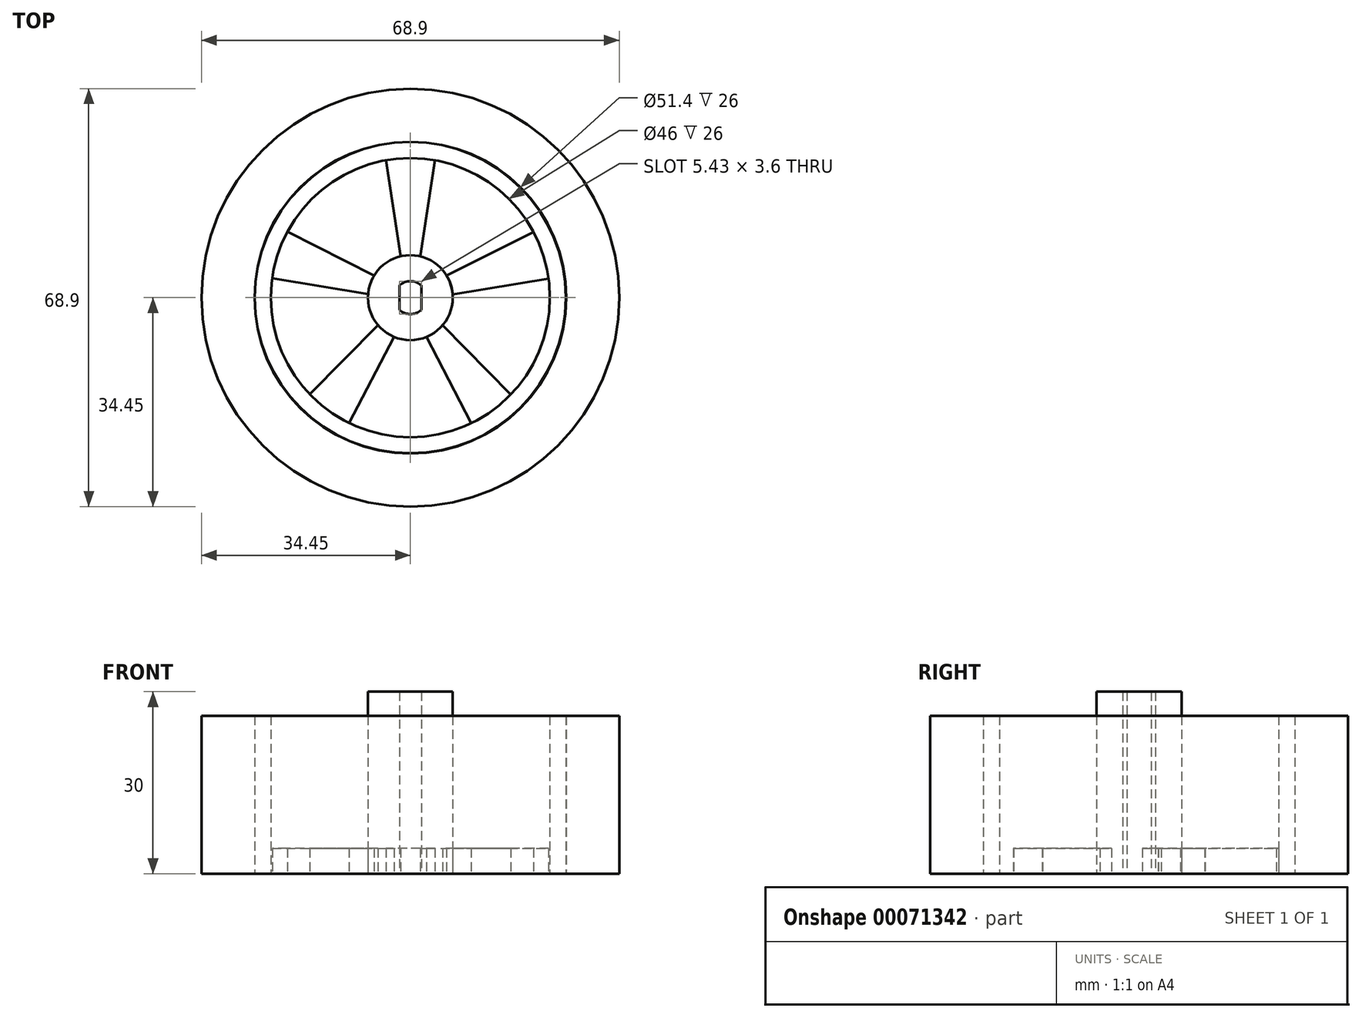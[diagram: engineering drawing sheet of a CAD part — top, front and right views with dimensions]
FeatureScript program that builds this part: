
annotation { "Feature Type Name" : "Feature", "Feature Type Description" : "" }
export const myFeature = defineFeature(function(context is Context, id is Id, definition is map)
    precondition{}
    {
        {
            var Q0;
            Q0=qCreatedBy(makeId("Top.planeOp"),FACE);
            var sketch = newSketch(context, id + "F0", { "sketchPlane" : qUnion([Q0])});
            skCircle(sketch, "E0", {"center": v(0, 0) * mm, "radius": 25.66 * mm});
            skCircle(sketch, "E1", {"center": v(0, 0) * mm, "radius": 23 * mm});
            skCircle(sketch, "E2", {"center": v(0, 0) * mm, "radius": 7 * mm});
            skArc(sketch, "E3", {"start": v(-1.8, -2.03) * mm, "mid": v(0, -2.71) * mm, "end": v(1.8, -2.03) * mm});
            skLineSegment(sketch, "E4.left", {"start": v(1.8, -2.03) * mm, "end": v(1.8, 2.03) * mm});
            skLineSegment(sketch, "E4.right", {"start": v(-1.8, -2.03) * mm, "end": v(-1.8, 2.03) * mm});
            skArc(sketch, "E5.trimOffspring", {"start": v(1.8, 2.03) * mm, "mid": v(0, 2.71) * mm, "end": v(-1.8, 2.03) * mm});
            skLineSegment(sketch, "E6", {"start": v(1.63, 6.8) * mm, "end": v(4.07, 22.64) * mm});
            skLineSegment(sketch, "E7", {"start": v(-4, 22.65) * mm, "end": v(-1.62, 6.8) * mm});
            skLineSegment(sketch, "E8.1.0", {"start": v(-22.78, 3.2) * mm, "end": v(-6.98, 0.56) * mm});
            skLineSegment(sketch, "E8.1.1", {"start": v(-5.97, 3.65) * mm, "end": v(-20.27, 10.87) * mm});
            skLineSegment(sketch, "E8.2.0", {"start": v(-10.08, -20.67) * mm, "end": v(-2.7, -6.46) * mm});
            skLineSegment(sketch, "E8.2.1", {"start": v(-5.32, -4.55) * mm, "end": v(-16.6, -15.92) * mm});
            skLineSegment(sketch, "E8.3.0", {"start": v(16.55, -15.97) * mm, "end": v(5.31, -4.56) * mm});
            skLineSegment(sketch, "E8.3.1", {"start": v(2.69, -6.46) * mm, "end": v(10.01, -20.7) * mm});
            skLineSegment(sketch, "E8.4.0", {"start": v(20.3, 10.8) * mm, "end": v(5.98, 3.65) * mm});
            skLineSegment(sketch, "E8.4.1", {"start": v(6.98, 0.56) * mm, "end": v(22.79, 3.12) * mm});
            skSolve(sketch);
        }
        {
            var Q0;
            Q0=qCreatedBy(makeId("Top.planeOp"),FACE);
            var sketch = newSketch(context, id + "F1", { "sketchPlane" : qUnion([Q0])});
            skCircle(sketch, "E9", {"center": v(0, 0) * mm, "radius": 34.44 * mm});
            skCircle(sketch, "E10", {"center": v(0, 0) * mm, "radius": 25.7 * mm});
            skSolve(sketch);
        }
        {
            var Q0;
            Q0=makeQuery(id+"F0.imprint","IMPRINT",FACE,{"disambiguationData":[TD([[makeQuery(id+"F0.imprint","IMPRINT",EDGE,{"derivedFrom":sQuery(id+"F0.wireOp",EDGE,"E2")}),1.0]])]});
            extrude(context, id + "F2", {"entities" : qUnion([Q0]), "depth" : 30 * mm});
        }
        {
            var Q0;
            Q0=makeQuery(id+"F0.imprint","IMPRINT",FACE,{"disambiguationData":[TD([[makeQuery(id+"F0.imprint","IMPRINT",EDGE,{"derivedFrom":sQuery(id+"F0.wireOp",EDGE,"E0")}),1.0]])]});
            extrude(context, id + "F3", {"entities" : qUnion([Q0]), "depth" : 26 * mm});
        }
        {
            var Q0;
            {var subQ0=sQuery(id+"F0.wireOp",EDGE,"E6");Q0=makeQuery(id+"F0.imprint","IMPRINT",FACE,{"disambiguationData":[TD([[makeQuery(id+"F0.imprint","IMPRINT",EDGE,{"derivedFrom":subQ0}),1.0]])]});}
            var Q1;
            {var subQ0=sQuery(id+"F0.wireOp",EDGE,"E8.3.0");Q1=makeQuery(id+"F0.imprint","IMPRINT",FACE,{"disambiguationData":[TD([[makeQuery(id+"F0.imprint","IMPRINT",EDGE,{"derivedFrom":subQ0}),1.0]])]});}
            var Q2;
            {var subQ0=sQuery(id+"F0.wireOp",EDGE,"E8.2.0");Q2=makeQuery(id+"F0.imprint","IMPRINT",FACE,{"disambiguationData":[TD([[makeQuery(id+"F0.imprint","IMPRINT",EDGE,{"derivedFrom":subQ0}),1.0]])]});}
            var Q3;
            {var subQ0=sQuery(id+"F0.wireOp",EDGE,"E8.1.0");Q3=makeQuery(id+"F0.imprint","IMPRINT",FACE,{"disambiguationData":[TD([[makeQuery(id+"F0.imprint","IMPRINT",EDGE,{"derivedFrom":subQ0}),1.0]])]});}
            var Q4;
            {var subQ0=sQuery(id+"F0.wireOp",EDGE,"E8.4.0");Q4=makeQuery(id+"F0.imprint","IMPRINT",FACE,{"disambiguationData":[TD([[makeQuery(id+"F0.imprint","IMPRINT",EDGE,{"derivedFrom":subQ0}),1.0]])]});}
            extrude(context, id + "F4", {"entities" : qUnion([Q0, Q1, Q2, Q3, Q4]), "depth" : 4.15 * mm});
        }
        {
            var Q0;
            Q0=makeQuery(id+"F1.imprint","IMPRINT",FACE,{"disambiguationData":[TD([[makeQuery(id+"F1.imprint","IMPRINT",EDGE,{"derivedFrom":sQuery(id+"F1.wireOp",EDGE,"E9")}),1.0]])]});
            extrude(context, id + "F5", {"entities" : qUnion([Q0]), "operationType" : NewBodyOperationType.ADD, "depth" : 26 * mm});
        }
    });
